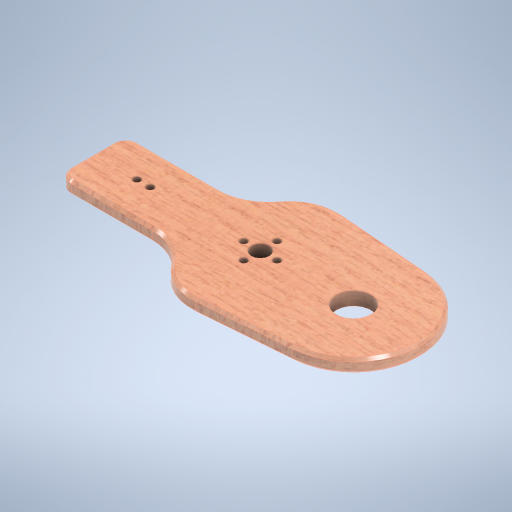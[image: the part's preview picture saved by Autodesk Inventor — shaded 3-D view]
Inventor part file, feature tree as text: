
AUTODESK INVENTOR PART (.ipt)
format: ipt  version: 2023 (Build 270158030, 158C)  size: 435,200 bytes
history: native  units: in
note: dims shown in document units (in); Inventor stores cm internally (conversion verified against a paired STEP export)
features: extrude x5, sketch x4, fillet x2, chamfer x1
ambient origin geometry x8: Origin, YZ Plane, XZ Plane, XY Plane, X Axis, Y Axis, Z Axis, Center Point
bodies: Solid1 (feature_tree)
feature tree (12):
  extrude  "Main"  Depth=6.2598in
  extrude  "Axis Holes"  Depth=1.9685in
  extrude  "Extrusion6"  Depth=0.3937in
  extrude  "Extrusion7"  Depth=0.3937in
  fillet  "Fillet1"  Radius=2.7559in
  fillet  "Fillet2"  Radius=2.0in
  chamfer  "Chamfer1"  Distance=0.2756in
  extrude  "Extrusion8"  Depth=0.3937in
  sketch  "Sketch1"  dims[d0=2.9528in d1=6.2598in]
  sketch  "Sketch5"  dims[d2=2.0in d3=1.9685in]
  sketch  "Sketch6"  dims[d4=0.3937in d5=0.0in d6=0.5315in]
  sketch  "Sketch7"  dims[d7=0.0in d8=0.0in d40=1.0236in d41=2.7559in d43=2.0in d44=0.2756in d45=0.3937in d46=0.2165in d47=0.0in d48=0.0in d49=2.0in d50=3.5433in d51=0.0in d52=0.0in d53=1.4537in d54=0.3937in d55=0.0787in d56=0.0787in d57=45.0deg d58=0.2165in d59=1.5748in d61=360.0deg d63=0.9843in d64=0.3937in d65=0.0in]
